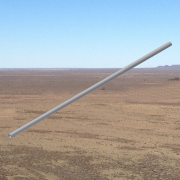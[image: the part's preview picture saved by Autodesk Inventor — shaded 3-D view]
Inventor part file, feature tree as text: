
AUTODESK INVENTOR PART (.ipt)
format: ipt  version: 2013 SP2 (Build 170200200, 200)  size: 122,880 bytes
history: native  units: in
note: dims shown in document units (in); Inventor stores cm internally (conversion verified against a paired STEP export)
features: extrude x1, sketch x1
ambient origin geometry x8: Origin, YZ Plane, XZ Plane, XY Plane, X Axis, Y Axis, Z Axis, Center Point
bodies: Solid1 (feature_tree)
feature tree (2):
  extrude  "Extrusion1"  Depth=23.0in TaperAngle=0.0deg
  sketch  "Sketch1"  dims[d0=0.5in d2=23.0in d3=0.0in]
